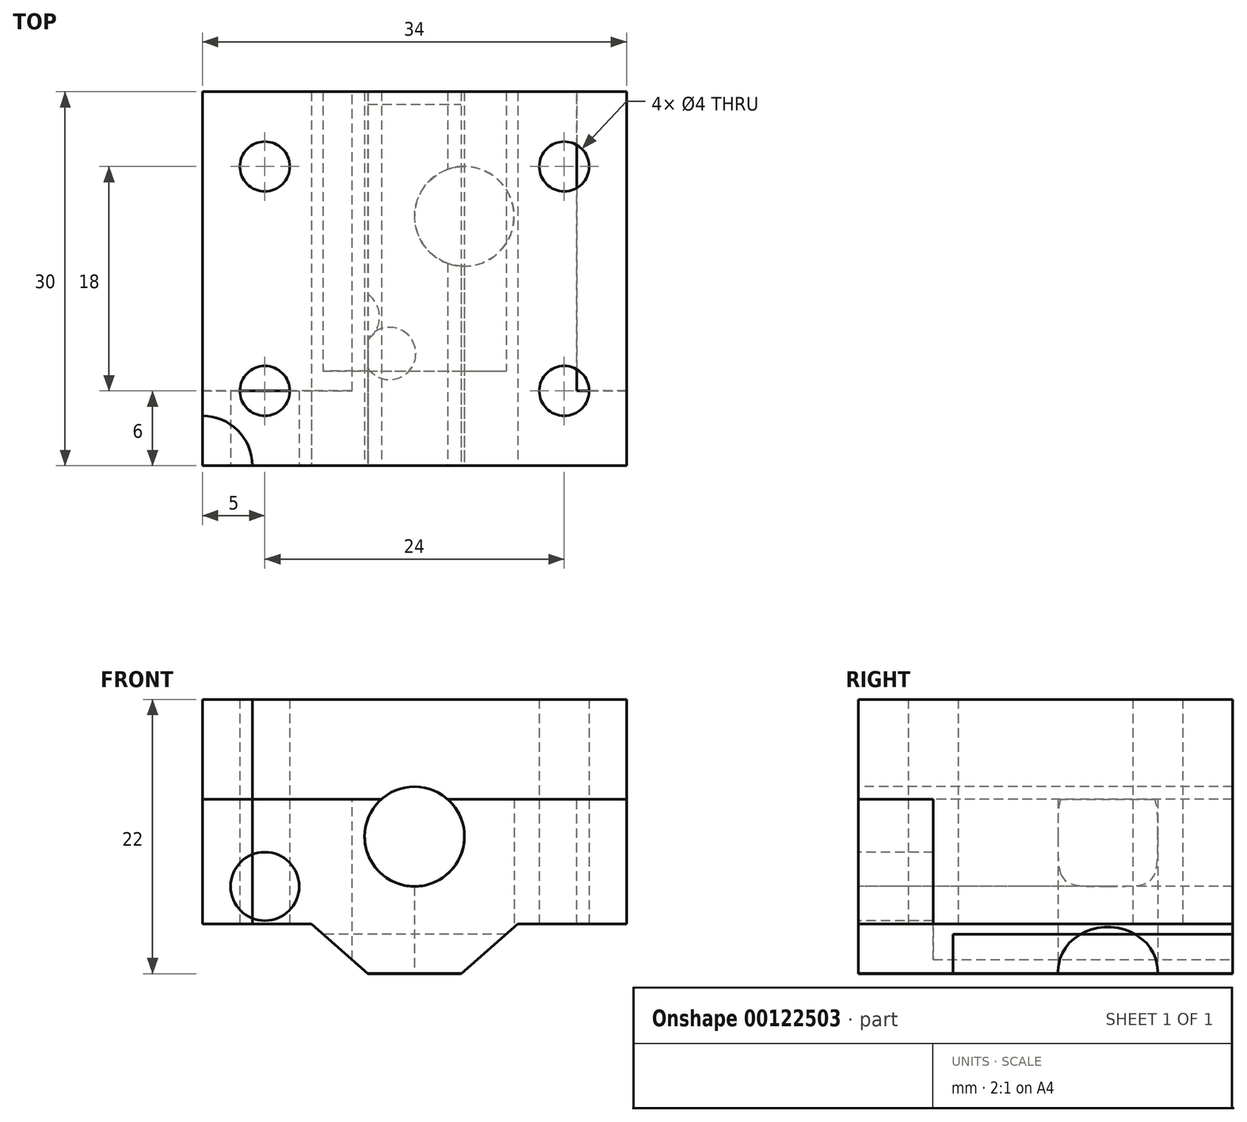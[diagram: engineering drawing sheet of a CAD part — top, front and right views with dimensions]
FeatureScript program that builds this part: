
annotation { "Feature Type Name" : "Feature", "Feature Type Description" : "" }
export const myFeature = defineFeature(function(context is Context, id is Id, definition is map)
    precondition{}
    {
        {
            var Q0;
            Q0=qCreatedBy(makeId("Top.planeOp"),FACE);
            var sketch = newSketch(context, id + "F0", { "sketchPlane" : qUnion([Q0])});
            skLineSegment(sketch, "E0.bottom", {"start": v(0, 0) * mm, "end": v(62, 0) * mm});
            skLineSegment(sketch, "E0.top", {"start": v(0, 62) * mm, "end": v(42, 62) * mm});
            skLineSegment(sketch, "E0.left", {"start": v(0, 0) * mm, "end": v(0, 62) * mm});
            skLineSegment(sketch, "E0.right", {"start": v(62, 0) * mm, "end": v(62, 42) * mm});
            skLineSegment(sketch, "E1", {"start": v(42, 42) * mm, "end": v(62, 42) * mm});
            skLineSegment(sketch, "E2", {"start": v(42, 42) * mm, "end": v(42, 62) * mm});
            skPoint(sketch, "E3", {"position": v(42, 42) * mm});
            skLineSegment(sketch, "E4", {"start": v(5.5, 62) * mm, "end": v(5.5, 0) * mm, "construction": true});
            skLineSegment(sketch, "E5", {"start": v(0, 5.5) * mm, "end": v(62, 5.5) * mm, "construction": true});
            skLineSegment(sketch, "E6", {"start": v(36.5, 62) * mm, "end": v(36.5, 0) * mm, "construction": true});
            skLineSegment(sketch, "E7", {"start": v(62, 36.5) * mm, "end": v(0, 36.5) * mm, "construction": true});
            skLineSegment(sketch, "E8", {"start": v(42, 52) * mm, "end": v(0, 52) * mm, "construction": true});
            skLineSegment(sketch, "E9", {"start": v(52, 42) * mm, "end": v(52, 0) * mm, "construction": true});
            skPoint(sketch, "E10", {"position": v(52, 36.5) * mm});
            skPoint(sketch, "E11", {"position": v(5.5, 5.5) * mm});
            skPoint(sketch, "E12", {"position": v(5.5, 36.5) * mm});
            skPoint(sketch, "E13", {"position": v(36.5, 36.5) * mm});
            skPoint(sketch, "E14", {"position": v(36.5, 5.5) * mm});
            skCircle(sketch, "E15", {"center": v(5.5, 36.5) * mm, "radius": 1.75 * mm});
            skCircle(sketch, "E16", {"center": v(36.5, 36.5) * mm, "radius": 1.75 * mm});
            skCircle(sketch, "E17", {"center": v(36.5, 5.5) * mm, "radius": 1.75 * mm});
            skCircle(sketch, "E18", {"center": v(5.5, 5.5) * mm, "radius": 1.75 * mm});
            skCircle(sketch, "E19", {"center": v(5.5, 52) * mm, "radius": 2.75 * mm});
            skCircle(sketch, "E20", {"center": v(36.5, 52) * mm, "radius": 2.75 * mm});
            skCircle(sketch, "E21", {"center": v(52, 36.5) * mm, "radius": 2.75 * mm});
            skCircle(sketch, "E22", {"center": v(52, 5.5) * mm, "radius": 2.75 * mm});
            skLineSegment(sketch, "E23", {"start": v(5.5, 5.5) * mm, "end": v(36.5, 36.5) * mm, "construction": true});
            skCircle(sketch, "E24", {"center": v(11.94, 11.94) * mm, "radius": 2.25 * mm});
            skSolve(sketch);
        }
        {
            var Q0;
            Q0=makeQuery(id+"F0.imprint","IMPRINT",FACE,{"disambiguationData":[TD([[makeQuery(id+"F0.imprint","IMPRINT",EDGE,{"derivedFrom":sQuery(id+"F0.wireOp",EDGE,"E0.bottom")}),1.0]])]});
            extrude(context, id + "F1", {"entities" : qUnion([Q0]), "depth" : 1 / 50.8 * mm});
        }
        {
            var Q0;
            Q0=qCreatedBy(makeId("Top.planeOp"),FACE);
            var sketch = newSketch(context, id + "F2", { "sketchPlane" : qUnion([Q0])});
            skLineSegment(sketch, "E25", {"start": v(0, 0) * mm, "end": v(0, 62) * mm});
            skLineSegment(sketch, "E26", {"start": v(0, 62) * mm, "end": v(62, 62) * mm});
            skLineSegment(sketch, "E27", {"start": v(62, 62) * mm, "end": v(62, 20) * mm});
            skLineSegment(sketch, "E28", {"start": v(62, 20) * mm, "end": v(42, 20) * mm});
            skLineSegment(sketch, "E29", {"start": v(42, 20) * mm, "end": v(42, 0) * mm});
            skLineSegment(sketch, "E30", {"start": v(42, 0) * mm, "end": v(0, 0) * mm});
            skLineSegment(sketch, "E31", {"start": v(42, 10) * mm, "end": v(0, 10) * mm, "construction": true});
            skLineSegment(sketch, "E32", {"start": v(52, 20) * mm, "end": v(52, 62) * mm, "construction": true});
            skLineSegment(sketch, "E33", {"start": v(0, 56.5) * mm, "end": v(62, 56.5) * mm, "construction": true});
            skLineSegment(sketch, "E34", {"start": v(0, 62) * mm, "end": v(42, 20) * mm, "construction": true});
            skLineSegment(sketch, "E35", {"start": v(5.5, 62) * mm, "end": v(5.5, 0) * mm, "construction": true});
            skLineSegment(sketch, "E36", {"start": v(0, 25.5) * mm, "end": v(62, 25.5) * mm, "construction": true});
            skLineSegment(sketch, "E37", {"start": v(36.5, 62) * mm, "end": v(36.5, 0) * mm, "construction": true});
            skPoint(sketch, "E38", {"position": v(5.5, 56.5) * mm});
            skPoint(sketch, "E39", {"position": v(36.5, 25.5) * mm});
            skCircle(sketch, "E40", {"center": v(5.5, 10) * mm, "radius": 2.75 * mm});
            skCircle(sketch, "E41", {"center": v(36.5, 10) * mm, "radius": 2.75 * mm});
            skCircle(sketch, "E42", {"center": v(52, 25.5) * mm, "radius": 2.75 * mm});
            skCircle(sketch, "E43", {"center": v(52, 56.5) * mm, "radius": 2.75 * mm});
            skPoint(sketch, "E44", {"position": v(21, 41) * mm});
            skPoint(sketch, "E45", {"position": v(13.93, 48.07) * mm});
            skPoint(sketch, "E46", {"position": v(28.07, 33.93) * mm});
            skCircle(sketch, "E47", {"center": v(13.93, 48.07) * mm, "radius": 4 * mm});
            skCircle(sketch, "E48", {"center": v(28.07, 33.93) * mm, "radius": 4 * mm});
            skSolve(sketch);
        }
        {
            var Q0;
            Q0=makeQuery(id+"F2.imprint","IMPRINT",FACE,{"disambiguationData":[TD([[makeQuery(id+"F2.imprint","IMPRINT",EDGE,{"derivedFrom":sQuery(id+"F2.wireOp",EDGE,"E25")}),-1.0]])]});
            extrude(context, id + "F3", {"entities" : qUnion([Q0]), "depth" : 1 / 50.8 * mm});
        }
        {
            var Q0;
            Q0=qCreatedBy(makeId("Top.planeOp"),FACE);
            var sketch = newSketch(context, id + "F4", { "sketchPlane" : qUnion([Q0])});
            skCircle(sketch, "E49", {"center": v(61.15, 63.66) * mm, "radius": 4 * mm});
            skSolve(sketch);
        }
        {
            var Q0;
            Q0=makeQuery(id+"F4.imprint","IMPRINT",FACE,{"disambiguationData":[TD([[makeQuery(id+"F4.imprint","IMPRINT",EDGE,{"derivedFrom":sQuery(id+"F4.wireOp",EDGE,"E49")}),1.0]])]});
            extrude(context, id + "F5", {"entities" : qUnion([Q0]), "depth" : 100 * mm});
        }
        {
            var Q0;
            Q0=qCreatedBy(makeId("Top.planeOp"),FACE);
            var sketch = newSketch(context, id + "F6", { "sketchPlane" : qUnion([Q0])});
            skLineSegment(sketch, "E50.bottom", {"start": v(0, 0) * mm, "end": v(62, 0) * mm});
            skLineSegment(sketch, "E50.top", {"start": v(0, 84) * mm, "end": v(62, 84) * mm});
            skLineSegment(sketch, "E50.left", {"start": v(0, 0) * mm, "end": v(0, 84) * mm});
            skLineSegment(sketch, "E50.right", {"start": v(62, 0) * mm, "end": v(62, 84) * mm});
            skLineSegment(sketch, "E51", {"start": v(52, 0) * mm, "end": v(52, 84) * mm, "construction": true});
            skLineSegment(sketch, "E52", {"start": v(62, 42) * mm, "end": v(0, 42) * mm, "construction": true});
            skLineSegment(sketch, "E53", {"start": v(52, 36.5) * mm, "end": v(62, 36.5) * mm, "construction": true});
            skLineSegment(sketch, "E54", {"start": v(62, 5.5) * mm, "end": v(52, 5.5) * mm, "construction": true});
            skLineSegment(sketch, "E55", {"start": v(52, 47.5) * mm, "end": v(62, 47.5) * mm, "construction": true});
            skLineSegment(sketch, "E56", {"start": v(52, 78.5) * mm, "end": v(62, 78.5) * mm, "construction": true});
            skCircle(sketch, "E57", {"center": v(52, 78.5) * mm, "radius": 2.75 * mm});
            skCircle(sketch, "E58", {"center": v(52, 47.5) * mm, "radius": 2.75 * mm});
            skCircle(sketch, "E59", {"center": v(52, 36.5) * mm, "radius": 2.75 * mm});
            skCircle(sketch, "E60", {"center": v(52, 5.5) * mm, "radius": 2.75 * mm});
            skPoint(sketch, "E61", {"position": v(52, 42) * mm});
            skLineSegment(sketch, "E62", {"start": v(9, 84) * mm, "end": v(9, 0) * mm, "construction": true});
            skLineSegment(sketch, "E63", {"start": v(33, 0) * mm, "end": v(33, 84) * mm, "construction": true});
            skLineSegment(sketch, "E64", {"start": v(0, 33) * mm, "end": v(62, 33) * mm, "construction": true});
            skLineSegment(sketch, "E65", {"start": v(0, 51) * mm, "end": v(62, 51) * mm, "construction": true});
            skLineSegment(sketch, "E66", {"start": v(0, 15) * mm, "end": v(62, 15) * mm, "construction": true});
            skLineSegment(sketch, "E67", {"start": v(0, 69) * mm, "end": v(62, 69) * mm, "construction": true});
            skCircle(sketch, "E68", {"center": v(9, 69) * mm, "radius": 2.1 * mm});
            skCircle(sketch, "E69", {"center": v(9, 51) * mm, "radius": 2.1 * mm});
            skCircle(sketch, "E70", {"center": v(9, 33) * mm, "radius": 2.1 * mm});
            skCircle(sketch, "E71", {"center": v(9, 15) * mm, "radius": 2.1 * mm});
            skCircle(sketch, "E72", {"center": v(33, 15) * mm, "radius": 2.1 * mm});
            skCircle(sketch, "E73", {"center": v(33, 33) * mm, "radius": 2.1 * mm});
            skCircle(sketch, "E74", {"center": v(33, 51) * mm, "radius": 2.1 * mm});
            skCircle(sketch, "E75", {"center": v(33, 69) * mm, "radius": 2.1 * mm});
            skLineSegment(sketch, "E76", {"start": v(0, 25) * mm, "end": v(62, 25) * mm, "construction": true});
            skLineSegment(sketch, "E77", {"start": v(0, 59) * mm, "end": v(62, 59) * mm, "construction": true});
            skCircle(sketch, "E78", {"center": v(33, 59) * mm, "radius": 4 * mm});
            skCircle(sketch, "E79", {"center": v(33, 25) * mm, "radius": 4 * mm});
            skSolve(sketch);
        }
        {
            var Q0;
            Q0=makeQuery(id+"F6.imprint","IMPRINT",FACE,{"disambiguationData":[TD([[makeQuery(id+"F6.imprint","IMPRINT",EDGE,{"derivedFrom":sQuery(id+"F6.wireOp",EDGE,"E50.bottom")}),1.0]])]});
            extrude(context, id + "F7", {"entities" : qUnion([Q0]), "depth" : 1 / 50.8 * mm});
        }
        {
            var Q0;
            Q0=qCreatedBy(makeId("Top.planeOp"),FACE);
            var sketch = newSketch(context, id + "F8", { "sketchPlane" : qUnion([Q0])});
            skLineSegment(sketch, "E80.bottom", {"start": v(0, 0) * mm, "end": v(5, 0) * mm});
            skLineSegment(sketch, "E80.left", {"start": v(0, 0) * mm, "end": v(0, 6) * mm});
            skLineSegment(sketch, "E80.right", {"start": v(42, 0) * mm, "end": v(42, 6) * mm});
            skLineSegment(sketch, "E81", {"start": v(12, 20) * mm, "end": v(30, 20) * mm, "construction": true});
            skLineSegment(sketch, "E82", {"start": v(21, 32.8) * mm, "end": v(21, 0) * mm, "construction": true});
            skLineSegment(sketch, "E83", {"start": v(12, 32.8) * mm, "end": v(21, 32.8) * mm});
            skLineSegment(sketch, "E84", {"start": v(21, 32.8) * mm, "end": v(30, 32.8) * mm});
            skLineSegment(sketch, "E85", {"start": v(0, 6) * mm, "end": v(12, 6) * mm});
            skLineSegment(sketch, "E86", {"start": v(12, 32.8) * mm, "end": v(12, 6) * mm});
            skLineSegment(sketch, "E87", {"start": v(30, 32.8) * mm, "end": v(30, 6) * mm});
            skPoint(sketch, "E88.orphan", {"position": v(0, 32.8) * mm});
            skPoint(sketch, "E89.orphan", {"position": v(42, 20) * mm});
            skLineSegment(sketch, "E90", {"start": v(0, 32.8) * mm, "end": v(12, 32.8) * mm, "construction": true});
            skCircle(sketch, "E91", {"center": v(21, 20) * mm, "radius": 4 * mm});
            skLineSegment(sketch, "E92", {"start": v(5, 0) * mm, "end": v(21, 0) * mm});
            skLineSegment(sketch, "E93", {"start": v(37, 0) * mm, "end": v(42, 0) * mm});
            skLineSegment(sketch, "E94", {"start": v(21, 0) * mm, "end": v(37, 0) * mm});
            skLineSegment(sketch, "E95", {"start": v(12, 6) * mm, "end": v(30, 6) * mm, "construction": true});
            skLineSegment(sketch, "E96", {"start": v(30, 6) * mm, "end": v(42, 6) * mm});
            skSolve(sketch);
        }
        {
            var Q0;
            Q0=makeQuery(id+"F8.imprint","IMPRINT",FACE,{"disambiguationData":[TD([[makeQuery(id+"F8.imprint","IMPRINT",EDGE,{"derivedFrom":sQuery(id+"F8.wireOp",EDGE,"E80.bottom")}),1.0]])]});
            extrude(context, id + "F9", {"entities" : qUnion([Q0]), "depth" : 14 * mm});
        }
        {
            var Q0;
            Q0=makeQuery(id+"F9.opExtrude","SWEPT_FACE",FACE,{"disambiguationData":[OSD([sQuery(id+"F8.wireOp",EDGE,"E80.bottom"),sQuery(id+"F8.wireOp",EDGE,"E92"),sQuery(id+"F8.wireOp",EDGE,"E93"),sQuery(id+"F8.wireOp",EDGE,"E94")])]});
            var sketch = newSketch(context, id + "F10", { "sketchPlane" : qUnion([Q0])});
            skLineSegment(sketch, "E97.bottom", {"start": v(0, 0) * mm, "end": v(42, 0) * mm});
            skLineSegment(sketch, "E97.top", {"start": v(0, 14) * mm, "end": v(42, 14) * mm});
            skLineSegment(sketch, "E97.left", {"start": v(0, 0) * mm, "end": v(0, 14) * mm});
            skLineSegment(sketch, "E97.right", {"start": v(42, 0) * mm, "end": v(42, 14) * mm});
            skLineSegment(sketch, "E98", {"start": v(0, 7) * mm, "end": v(42, 7) * mm, "construction": true});
            skLineSegment(sketch, "E99", {"start": v(21, 14) * mm, "end": v(21, 0) * mm, "construction": true});
            skLineSegment(sketch, "E100", {"start": v(5, 14) * mm, "end": v(5, 0) * mm, "construction": true});
            skLineSegment(sketch, "E101", {"start": v(37, 14) * mm, "end": v(37, 0) * mm, "construction": true});
            skCircle(sketch, "E102", {"center": v(5, 7) * mm, "radius": 2.75 * mm});
            skCircle(sketch, "E103", {"center": v(37, 7) * mm, "radius": 2.75 * mm});
            skSolve(sketch);
        }
        {
            var Q0;
            Q0=makeQuery(id+"F10.imprint","IMPRINT",FACE,{"disambiguationData":[TD([[makeQuery(id+"F10.imprint","IMPRINT",EDGE,{"derivedFrom":sQuery(id+"F10.wireOp",EDGE,"E102")}),1.0]])]});
            var Q1;
            Q1=makeQuery(id+"F10.imprint","IMPRINT",FACE,{"disambiguationData":[TD([[makeQuery(id+"F10.imprint","IMPRINT",EDGE,{"derivedFrom":sQuery(id+"F10.wireOp",EDGE,"E103")}),1.0]])]});
            var Q2;
            Q2=sQuery(id+"F10.wireOp",EDGE,"E102");
            var Q3;
            Q3=sQuery(id+"F10.wireOp",EDGE,"E103");
            var Q4;
            Q4=makeQuery(id+"F9.opExtrude","SWEPT_FACE",FACE,{"disambiguationData":[OSD([sQuery(id+"F8.wireOp",EDGE,"E85")])]});
            extrude(context, id + "F11", {"entities" : qUnion([Q0, Q1]), "operationType" : NewBodyOperationType.REMOVE, "surfaceEntities" : qUnion([Q2, Q3]), "endBound" : BoundingType.UP_TO_SURFACE, "oppositeDirection" : true, "endBoundEntityFace" : qUnion([Q4]), "depth" : 25 * mm});
        }
        {
            var Q0;
            Q0=qCreatedBy(makeId("Top.planeOp"),FACE);
            var sketch = newSketch(context, id + "F12", { "sketchPlane" : qUnion([Q0])});
            skLineSegment(sketch, "E104.bottom", {"start": v(0, 0) * mm, "end": v(48, 0) * mm, "construction": true});
            skLineSegment(sketch, "E104.top", {"start": v(0, 84) * mm, "end": v(48, 84) * mm});
            skLineSegment(sketch, "E104.left", {"start": v(0, 0) * mm, "end": v(0, 84) * mm});
            skLineSegment(sketch, "E104.right", {"start": v(48, 0) * mm, "end": v(48, 84) * mm});
            skLineSegment(sketch, "E105", {"start": v(0, 42) * mm, "end": v(48, 42) * mm, "construction": true});
            skCircle(sketch, "E106", {"center": v(24, 42) * mm, "radius": 3 * mm});
            skLineSegment(sketch, "E107", {"start": v(24, 42) * mm, "end": v(24, -20) * mm, "construction": true});
            skLineSegment(sketch, "E108", {"start": v(24, 42) * mm, "end": v(24, 84) * mm, "construction": true});
            skLineSegment(sketch, "E109", {"start": v(24, 63) * mm, "end": v(48, 63) * mm, "construction": true});
            skLineSegment(sketch, "E110", {"start": v(24, 63) * mm, "end": v(0, 63) * mm, "construction": true});
            skLineSegment(sketch, "E111", {"start": v(24, 21) * mm, "end": v(0, 21) * mm, "construction": true});
            skLineSegment(sketch, "E112", {"start": v(24, 21) * mm, "end": v(48, 21) * mm, "construction": true});
            skLineSegment(sketch, "E113", {"start": v(33, 84) * mm, "end": v(33, 0) * mm, "construction": true});
            skLineSegment(sketch, "E114", {"start": v(15, 0) * mm, "end": v(15, 84) * mm, "construction": true});
            skLineSegment(sketch, "E115", {"start": v(48, 75) * mm, "end": v(0, 75) * mm, "construction": true});
            skLineSegment(sketch, "E116", {"start": v(0, 51) * mm, "end": v(48, 51) * mm, "construction": true});
            skLineSegment(sketch, "E117", {"start": v(48, 33) * mm, "end": v(0, 33) * mm, "construction": true});
            skLineSegment(sketch, "E118", {"start": v(0, 9) * mm, "end": v(48, 9) * mm, "construction": true});
            skCircle(sketch, "E119", {"center": v(15, 75) * mm, "radius": 2.1 * mm});
            skCircle(sketch, "E120", {"center": v(33, 75) * mm, "radius": 2.1 * mm});
            skCircle(sketch, "E121", {"center": v(33, 51) * mm, "radius": 2.1 * mm});
            skCircle(sketch, "E122", {"center": v(15, 51) * mm, "radius": 2.1 * mm});
            skCircle(sketch, "E123", {"center": v(15, 33) * mm, "radius": 2.1 * mm});
            skCircle(sketch, "E124", {"center": v(33, 33) * mm, "radius": 2.1 * mm});
            skCircle(sketch, "E125", {"center": v(15, 9) * mm, "radius": 2.1 * mm});
            skCircle(sketch, "E126", {"center": v(33, 9) * mm, "radius": 2.1 * mm});
            skLineSegment(sketch, "E127", {"start": v(0, 36) * mm, "end": v(48, 36) * mm, "construction": true});
            skLineSegment(sketch, "E128", {"start": v(48, 48) * mm, "end": v(0, 48) * mm, "construction": true});
            skLineSegment(sketch, "E129", {"start": v(7, 84) * mm, "end": v(7, 0) * mm, "construction": true});
            skLineSegment(sketch, "E130", {"start": v(41, 0) * mm, "end": v(41, 84) * mm, "construction": true});
            skCircle(sketch, "E131", {"center": v(7, 48) * mm, "radius": 4 * mm});
            skCircle(sketch, "E132", {"center": v(41, 48) * mm, "radius": 4 * mm});
            skCircle(sketch, "E133", {"center": v(41, 36) * mm, "radius": 4 * mm});
            skCircle(sketch, "E134", {"center": v(7, 36) * mm, "radius": 4 * mm});
            skLineSegment(sketch, "E135", {"start": v(0, 0) * mm, "end": v(0, -20) * mm});
            skLineSegment(sketch, "E136", {"start": v(0, -20) * mm, "end": v(24, -20) * mm});
            skLineSegment(sketch, "E137", {"start": v(48, -20) * mm, "end": v(48, 0) * mm});
            skPoint(sketch, "E138.orphan", {"position": v(24, 0) * mm});
            skLineSegment(sketch, "E139", {"start": v(0, -10) * mm, "end": v(48, -10) * mm, "construction": true});
            skCircle(sketch, "E140", {"center": v(24, -10) * mm, "radius": 7.5 * mm});
            skLineSegment(sketch, "E141", {"start": v(24, -20) * mm, "end": v(48, -20) * mm});
            skLineSegment(sketch, "E142", {"start": v(12, -20) * mm, "end": v(12, 0) * mm, "construction": true});
            skLineSegment(sketch, "E143", {"start": v(36, -20) * mm, "end": v(36, 0) * mm, "construction": true});
            skCircle(sketch, "E144", {"center": v(12, -10) * mm, "radius": 2.5 * mm});
            skCircle(sketch, "E145", {"center": v(36, -10) * mm, "radius": 2.5 * mm});
            skSolve(sketch);
        }
        {
            var Q0;
            Q0=makeQuery(id+"F12.imprint","IMPRINT",FACE,{"disambiguationData":[TD([[makeQuery(id+"F12.imprint","IMPRINT",EDGE,{"derivedFrom":sQuery(id+"F12.wireOp",EDGE,"E104.top")}),-1.0]])]});
            extrude(context, id + "F13", {"entities" : qUnion([Q0]), "depth" : 1 / 50.8 * mm});
        }
        {
            var Q0;
            Q0=makeQuery(id+"F12.imprint","IMPRINT",FACE,{"disambiguationData":[TD([[makeQuery(id+"F12.imprint","IMPRINT",EDGE,{"derivedFrom":sQuery(id+"F12.wireOp",EDGE,"E104.top")}),-1.0]])]});
            var sketch = newSketch(context, id + "F14", { "sketchPlane" : qUnion([Q0])});
            skLineSegment(sketch, "E146.bottom", {"start": v(0, 0) * mm, "end": v(48, 0) * mm});
            skLineSegment(sketch, "E146.top", {"start": v(0, -20) * mm, "end": v(48, -20) * mm});
            skLineSegment(sketch, "E146.left", {"start": v(0, 0) * mm, "end": v(0, -20) * mm});
            skLineSegment(sketch, "E146.right", {"start": v(48, 0) * mm, "end": v(48, -20) * mm});
            skCircle(sketch, "E147", {"center": v(24, -10) * mm, "radius": 3 * mm});
            skCircle(sketch, "E148", {"center": v(36, -10) * mm, "radius": 2.25 * mm});
            skCircle(sketch, "E149", {"center": v(12, -10) * mm, "radius": 2.25 * mm});
            skSolve(sketch);
        }
        {
            var Q0;
            Q0=makeQuery(id+"F14.imprint","IMPRINT",FACE,{"disambiguationData":[TD([[makeQuery(id+"F14.imprint","IMPRINT",EDGE,{"derivedFrom":sQuery(id+"F14.wireOp",EDGE,"E149")}),-1.0]])]});
            var Q1;
            Q1=makeQuery(id+"F14.imprint","IMPRINT",FACE,{"disambiguationData":[TD([[makeQuery(id+"F14.imprint","IMPRINT",EDGE,{"derivedFrom":sQuery(id+"F14.wireOp",EDGE,"E146.bottom")}),-1.0]])]});
            var Q2;
            Q2=makeQuery(id+"F14.imprint","IMPRINT",FACE,{"disambiguationData":[TD([[makeQuery(id+"F14.imprint","IMPRINT",EDGE,{"derivedFrom":sQuery(id+"F14.wireOp",EDGE,"E147")}),-1.0]])]});
            var Q3;
            Q3=makeQuery(id+"F14.imprint","IMPRINT",FACE,{"disambiguationData":[TD([[makeQuery(id+"F14.imprint","IMPRINT",EDGE,{"derivedFrom":sQuery(id+"F14.wireOp",EDGE,"E148")}),-1.0]])]});
            extrude(context, id + "F15", {"entities" : qUnion([Q0, Q1, Q2, Q3]), "depth" : 1 / 50.8 * mm});
        }
        {
            var Q0;
            Q0=makeQuery(id+"F14.imprint","IMPRINT",FACE,{"disambiguationData":[TD([[makeQuery(id+"F14.imprint","IMPRINT",EDGE,{"derivedFrom":sQuery(id+"F14.wireOp",EDGE,"E146.bottom")}),-1.0]])]});
            var sketch = newSketch(context, id + "F16", { "sketchPlane" : qUnion([Q0])});
            skLineSegment(sketch, "E150.bottom", {"start": v(0, 0) * mm, "end": v(48, 0) * mm});
            skLineSegment(sketch, "E150.top", {"start": v(0, -20) * mm, "end": v(48, -20) * mm});
            skLineSegment(sketch, "E150.left", {"start": v(0, 0) * mm, "end": v(0, -20) * mm});
            skLineSegment(sketch, "E150.right", {"start": v(48, 0) * mm, "end": v(48, -20) * mm});
            skCircle(sketch, "E151", {"center": v(12, -10) * mm, "radius": 2.5 * mm});
            skCircle(sketch, "E152", {"center": v(24, -10) * mm, "radius": 7.5 * mm});
            skCircle(sketch, "E153", {"center": v(36, -10) * mm, "radius": 2.5 * mm});
            skSolve(sketch);
        }
        {
            var Q0;
            Q0=makeQuery(id+"F16.imprint","IMPRINT",FACE,{"disambiguationData":[TD([[makeQuery(id+"F16.imprint","IMPRINT",EDGE,{"derivedFrom":sQuery(id+"F16.wireOp",EDGE,"E150.bottom")}),-1.0]])]});
            extrude(context, id + "F17", {"entities" : qUnion([Q0]), "depth" : 1 / 50.8 * mm});
        }
        {
            var Q0;
            Q0=makeQuery(id+"F12.imprint","IMPRINT",FACE,{"disambiguationData":[TD([[makeQuery(id+"F12.imprint","IMPRINT",EDGE,{"derivedFrom":sQuery(id+"F12.wireOp",EDGE,"E104.top")}),-1.0]])]});
            var sketch = newSketch(context, id + "F18", { "sketchPlane" : qUnion([Q0])});
            skCircle(sketch, "E154", {"center": v(7, 48) * mm, "radius": 4 * mm});
            skCircle(sketch, "E155", {"center": v(41, 48) * mm, "radius": 4 * mm});
            skCircle(sketch, "E156", {"center": v(41, 36) * mm, "radius": 4 * mm});
            skCircle(sketch, "E157", {"center": v(7, 36) * mm, "radius": 4 * mm});
            skLineSegment(sketch, "E158.bottom", {"start": v(0, 55) * mm, "end": v(48, 55) * mm});
            skLineSegment(sketch, "E158.top", {"start": v(0, 29) * mm, "end": v(48, 29) * mm});
            skLineSegment(sketch, "E158.left", {"start": v(0, 55) * mm, "end": v(0, 29) * mm});
            skLineSegment(sketch, "E158.right", {"start": v(48, 55) * mm, "end": v(48, 29) * mm});
            skLineSegment(sketch, "E159", {"start": v(48, 42) * mm, "end": v(0, 42) * mm, "construction": true});
            skLineSegment(sketch, "E160", {"start": v(24, 55) * mm, "end": v(24, 29) * mm, "construction": true});
            skCircle(sketch, "E161", {"center": v(24, 42) * mm, "radius": 7.5 * mm});
            skSolve(sketch);
        }
        {
            var Q0;
            Q0 = qSketchRegion(id + "F18", true);
            extrude(context, id + "F19", {"entities" : qUnion([Q0]), "depth" : 1 / 50.8 * mm});
        }
        {
            var Q0;
            Q0=qCreatedBy(makeId("Top.planeOp"),FACE);
            var sketch = newSketch(context, id + "F20", { "sketchPlane" : qUnion([Q0])});
            skLineSegment(sketch, "E162.bottom", {"start": v(-59.83, 7.1) * mm, "end": v(-54.83, 7.1) * mm});
            skLineSegment(sketch, "E162.top", {"start": v(-23.08, 37.1) * mm, "end": v(3.67, 37.1) * mm});
            skLineSegment(sketch, "E162.left", {"start": v(-59.83, 7.1) * mm, "end": v(-59.83, 17.1) * mm});
            skLineSegment(sketch, "E162.right", {"start": v(67.17, 7.1) * mm, "end": v(67.17, 17.1) * mm});
            skLineSegment(sketch, "E163", {"start": v(-54.83, 7.6) * mm, "end": v(62.17, 7.6) * mm});
            skLineSegment(sketch, "E164.trimOffspring", {"start": v(62.17, 7.1) * mm, "end": v(67.17, 7.1) * mm});
            skLineSegment(sketch, "E165", {"start": v(-54.83, 22.1) * mm, "end": v(-33.08, 22.1) * mm});
            skLineSegment(sketch, "E166", {"start": v(3.67, 37.1) * mm, "end": v(30.42, 37.1) * mm});
            skLineSegment(sketch, "E167", {"start": v(40.42, 22.1) * mm, "end": v(62.17, 22.1) * mm});
            skLineSegment(sketch, "E168", {"start": v(-28.08, 32.1) * mm, "end": v(-28.08, 27.1) * mm});
            skLineSegment(sketch, "E169", {"start": v(35.42, 32.1) * mm, "end": v(35.42, 27.1) * mm});
            skLineSegment(sketch, "E170", {"start": v(-54.83, 7.6) * mm, "end": v(-54.83, 7.1) * mm});
            skLineSegment(sketch, "E171", {"start": v(62.17, 7.6) * mm, "end": v(62.17, 7.1) * mm});
            skPoint(sketch, "E172.visualSharp", {"position": v(-59.83, 22.1) * mm});
            skArc(sketch, "E172.filletArc", {"start": v(-54.83, 22.1) * mm, "mid": v(-58.37, 20.63) * mm, "end": v(-59.83, 17.1) * mm});
            skPoint(sketch, "E173.visualSharp", {"position": v(-28.08, 37.1) * mm});
            skArc(sketch, "E173.filletArc", {"start": v(-23.08, 37.1) * mm, "mid": v(-26.62, 35.63) * mm, "end": v(-28.08, 32.1) * mm});
            skPoint(sketch, "E174.visualSharp", {"position": v(-28.08, 22.1) * mm});
            skArc(sketch, "E174.filletArc", {"start": v(-33.08, 22.1) * mm, "mid": v(-29.55, 23.56) * mm, "end": v(-28.08, 27.1) * mm});
            skPoint(sketch, "E175.visualSharp", {"position": v(35.42, 37.1) * mm});
            skArc(sketch, "E175.filletArc", {"start": v(35.42, 32.1) * mm, "mid": v(33.95, 35.63) * mm, "end": v(30.42, 37.1) * mm});
            skPoint(sketch, "E176.visualSharp", {"position": v(35.42, 22.1) * mm});
            skArc(sketch, "E176.filletArc", {"start": v(35.42, 27.1) * mm, "mid": v(36.88, 23.56) * mm, "end": v(40.42, 22.1) * mm});
            skPoint(sketch, "E177.visualSharp", {"position": v(67.17, 22.1) * mm});
            skArc(sketch, "E177.filletArc", {"start": v(67.17, 17.1) * mm, "mid": v(65.7, 20.63) * mm, "end": v(62.17, 22.1) * mm});
            skSolve(sketch);
        }
        {
            var Q0;
            Q0=makeQuery(id+"F20.imprint","IMPRINT",FACE,{"disambiguationData":[TD([[makeQuery(id+"F20.imprint","IMPRINT",EDGE,{"derivedFrom":sQuery(id+"F20.wireOp",EDGE,"E162.bottom")}),1.0]])]});
            extrude(context, id + "F21", {"entities" : qUnion([Q0]), "depth" : 3.17 * mm});
        }
        {
            var Q0;
            Q0=qCreatedBy(makeId("Top.planeOp"),FACE);
            var sketch = newSketch(context, id + "F22", { "sketchPlane" : qUnion([Q0])});
            skLineSegment(sketch, "E178.bottom", {"start": v(0, 0) * mm, "end": v(34, 0) * mm});
            skLineSegment(sketch, "E178.top", {"start": v(0, 30) * mm, "end": v(34, 30) * mm});
            skLineSegment(sketch, "E178.left", {"start": v(0, 0) * mm, "end": v(0, 30) * mm});
            skLineSegment(sketch, "E178.right", {"start": v(34, 0) * mm, "end": v(34, 30) * mm});
            skLineSegment(sketch, "E179", {"start": v(0, 15) * mm, "end": v(34, 15) * mm, "construction": true});
            skLineSegment(sketch, "E180", {"start": v(17, 0) * mm, "end": v(17, 30) * mm, "construction": true});
            skLineSegment(sketch, "E181.bottom", {"start": v(5, 24) * mm, "end": v(29, 24) * mm, "construction": true});
            skLineSegment(sketch, "E181.top", {"start": v(5, 6) * mm, "end": v(29, 6) * mm, "construction": true});
            skLineSegment(sketch, "E181.left", {"start": v(5, 24) * mm, "end": v(5, 6) * mm, "construction": true});
            skLineSegment(sketch, "E181.right", {"start": v(29, 24) * mm, "end": v(29, 6) * mm, "construction": true});
            skPoint(sketch, "E182", {"position": v(17, 24) * mm});
            skPoint(sketch, "E183", {"position": v(29, 15) * mm});
            skCircle(sketch, "E184", {"center": v(5, 24) * mm, "radius": 2 * mm});
            skCircle(sketch, "E185", {"center": v(29, 24) * mm, "radius": 2 * mm});
            skCircle(sketch, "E186", {"center": v(29, 6) * mm, "radius": 2 * mm});
            skCircle(sketch, "E187", {"center": v(5, 6) * mm, "radius": 2 * mm});
            skSolve(sketch);
        }
        {
            var Q0;
            Q0=makeQuery(id+"F22.imprint","IMPRINT",FACE,{"disambiguationData":[TD([[makeQuery(id+"F22.imprint","IMPRINT",EDGE,{"derivedFrom":sQuery(id+"F22.wireOp",EDGE,"E178.bottom")}),1.0]])]});
            extrude(context, id + "F23", {"entities" : qUnion([Q0]), "depth" : 22 * mm});
        }
        {
            var Q0;
            Q0=qCreatedBy(makeId("Top.planeOp"),FACE);
            var sketch = newSketch(context, id + "F24", { "sketchPlane" : qUnion([Q0])});
            skCircle(sketch, "E188", {"center": v(0, 0) * mm, "radius": 4 * mm});
            skSolve(sketch);
        }
        {
            var Q0;
            Q0=makeQuery(id+"F24.imprint","IMPRINT",FACE,{"disambiguationData":[TD([[makeQuery(id+"F24.imprint","IMPRINT",EDGE,{"derivedFrom":sQuery(id+"F24.wireOp",EDGE,"E188")}),1.0]])]});
            extrude(context, id + "F25", {"entities" : qUnion([Q0]), "depth" : 400 * mm});
        }
        {
            var Q0;
            Q0=makeQuery(id+"F23.opExtrude","SWEPT_FACE",FACE,{"disambiguationData":[OSD([sQuery(id+"F22.wireOp",EDGE,"E178.bottom")])]});
            var sketch = newSketch(context, id + "F26", { "sketchPlane" : qUnion([Q0])});
            skLineSegment(sketch, "E189.bottom", {"start": v(0, 22) * mm, "end": v(34, 22) * mm});
            skLineSegment(sketch, "E189.top", {"start": v(0, 0) * mm, "end": v(34, 0) * mm});
            skLineSegment(sketch, "E189.left", {"start": v(0, 22) * mm, "end": v(0, 0) * mm});
            skLineSegment(sketch, "E189.right", {"start": v(34, 22) * mm, "end": v(34, 0) * mm});
            skLineSegment(sketch, "E190", {"start": v(17, 22) * mm, "end": v(17, 0) * mm, "construction": true});
            skLineSegment(sketch, "E191", {"start": v(0, 11) * mm, "end": v(34, 11) * mm, "construction": true});
            skCircle(sketch, "E192", {"center": v(17, 11) * mm, "radius": 4 * mm});
            skLineSegment(sketch, "E193", {"start": v(0, 4) * mm, "end": v(34, 4) * mm, "construction": true});
            skLineSegment(sketch, "E194", {"start": v(0, 4) * mm, "end": v(8.72, 4) * mm});
            skLineSegment(sketch, "E195", {"start": v(8.72, 4) * mm, "end": v(13.27, 0) * mm});
            skLineSegment(sketch, "E196.MirrorCS", {"start": v(25.28, 4) * mm, "end": v(20.73, 0) * mm});
            skLineSegment(sketch, "E197", {"start": v(25.28, 4) * mm, "end": v(34, 4) * mm});
            skSolve(sketch);
        }
        {
            var Q0;
            {var subQ1=sQuery(id+"F26.wireOp",EDGE,"E189.bottom");Q0=makeQuery(id+"F26.imprint","IMPRINT",FACE,{"disambiguationData":[TD([[makeQuery(id+"F26.imprint","IMPRINT",EDGE,{"derivedFrom":subQ1}),-1.0]])]});}
            var Q1;
            Q1=makeQuery(id+"F23.opExtrude","SWEPT_FACE",FACE,{"disambiguationData":[OSD([sQuery(id+"F22.wireOp",EDGE,"E178.top")])]});
            extrude(context, id + "F27", {"entities" : qUnion([Q0]), "operationType" : NewBodyOperationType.INTERSECT, "endBound" : BoundingType.UP_TO_SURFACE, "oppositeDirection" : true, "endBoundEntityFace" : qUnion([Q1]), "depth" : 25 * mm});
        }
    });
